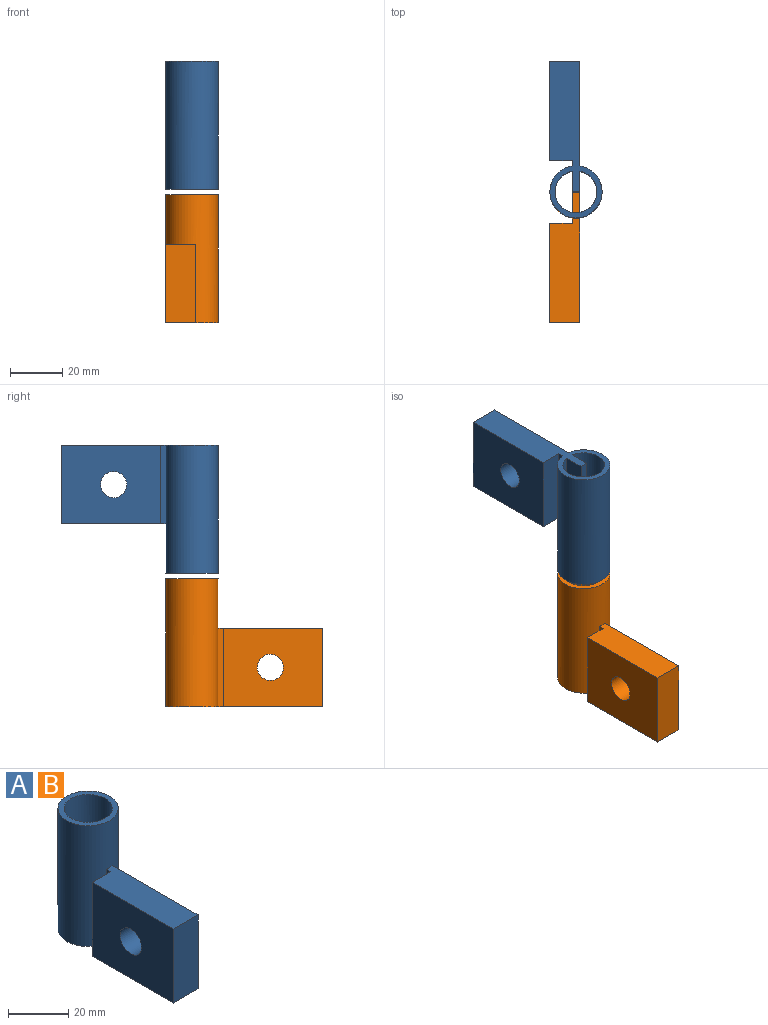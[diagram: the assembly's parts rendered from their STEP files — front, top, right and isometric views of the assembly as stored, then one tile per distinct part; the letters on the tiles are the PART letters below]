
ASSEMBLY  parts=2 mates=1
PART A: 15 faces, bbox 20x60x49 mm
  f0: plane 30x2.11mm, normal (-1,0,0), area 63.4mm2, adj f2,f4,f7,f13
  f1: cylinder r=8mm len=49mm, axis (0,0,-1), area 2372.5mm2, adj f3,f4,f8,f10,f11
  f2: cylinder r=10mm len=49mm, axis (0,0,-1), area 2988.4mm2, adj f0,f3,f4,f6,f7
  f3: plane 20x20mm, normal (0,0,1), area 113.1mm2, adj f1,f2
  f4: plane 60x20mm, normal (0,0,-1), area 580.1mm2, adj f0,f1,f2,f5,f6,f9,f10,f11
  f5: plane 30x11.5mm, normal (0,-1,0), area 345mm2, adj f4,f6,f7,f14
  f6: plane 40.11x30mm, normal (1,0,0), area 1124.9mm2, adj f2,f4,f5,f7,f12
  f7: plane 40.11x11.5mm, normal (0,0,1), area 443.1mm2, adj f0,f2,f5,f6,f13,f14
  f8: plane 8x3mm, normal (0,0,1), area 23.9mm2, adj f1,f9,f10,f11
  f9: plane 30x3mm, normal (0,1,0), area 90mm2, adj f4,f8,f10,f11
  f10: plane 30x7.86mm, normal (1,0,0), area 235.7mm2, adj f1,f4,f8,f9
  f11: plane 30x7.86mm, normal (-1,0,0), area 235.7mm2, adj f1,f4,f8,f9
  f12: cylinder r=5mm len=11.5mm, axis (1,0,0), area 361.3mm2, adj f6,f14
  f13: plane 30x8.5mm, normal (0,1,0), area 255mm2, adj f0,f4,f7,f14
  f14: plane 38x30mm, normal (-1,0,0), area 1061.5mm2, adj f4,f5,f7,f12,f13
PART B: same geometry as A
PLACE A rot(axis=(1,0,0),180deg) t=(0.01,23.1,62.14)mm
PLACE B t=(0.01,23.1,-37.86)mm fixed
MATE revolute A.f1 <-> B.f1  axis (0,0,1) through (0.01,23.1,13.14)mm
